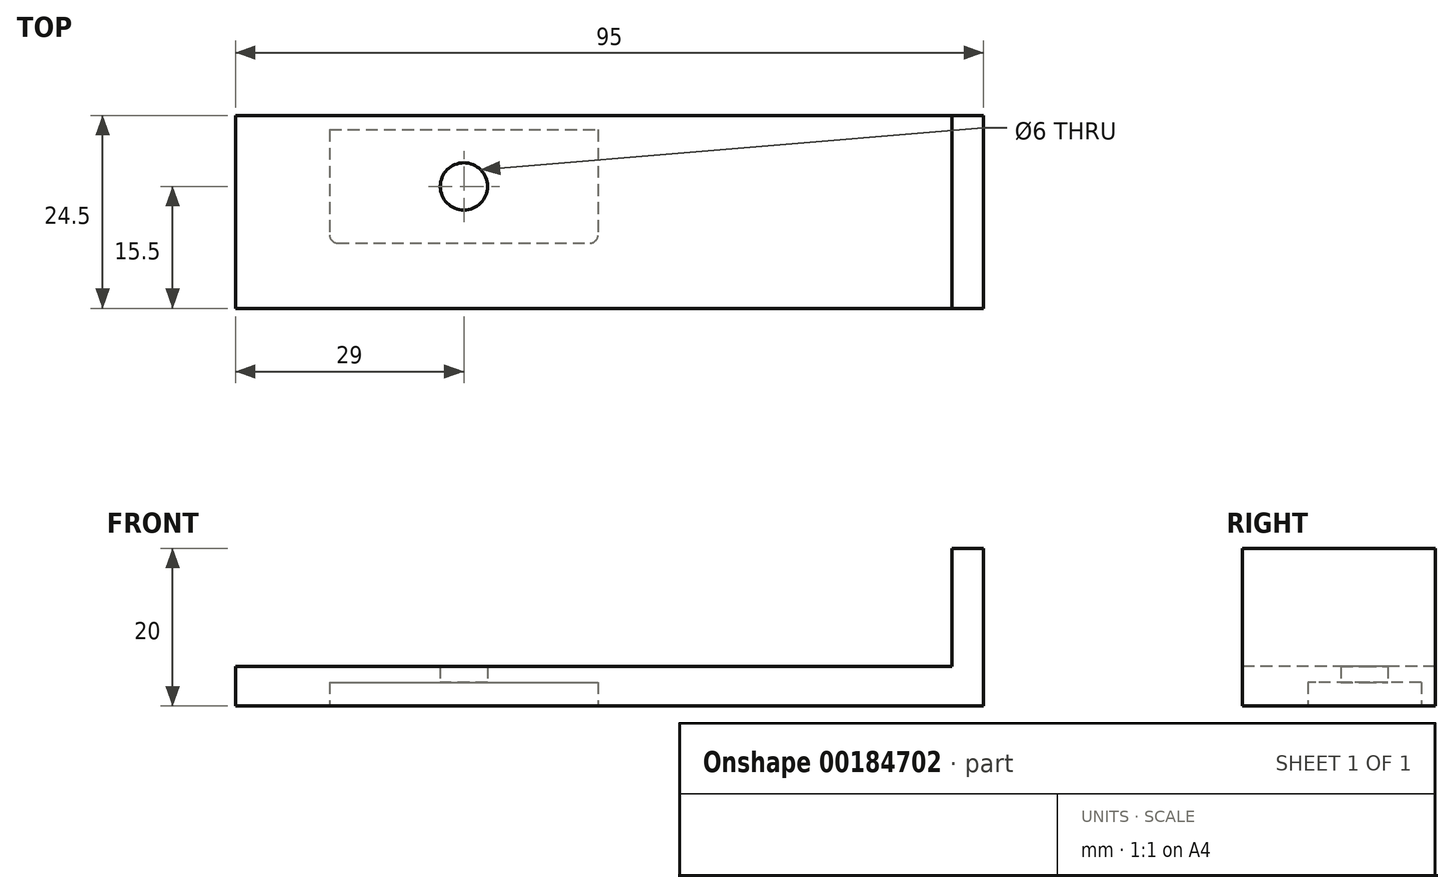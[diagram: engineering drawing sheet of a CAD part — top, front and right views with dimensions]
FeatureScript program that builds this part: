
annotation { "Feature Type Name" : "Feature", "Feature Type Description" : "" }
export const myFeature = defineFeature(function(context is Context, id is Id, definition is map)
    precondition{}
    {
        {
            var Q0;
            Q0=qCreatedBy(makeId("Top.planeOp"),FACE);
            var sketch = newSketch(context, id + "F0", { "sketchPlane" : qUnion([Q0])});
            skLineSegment(sketch, "E0.bottom", {"start": v(0, 0) * mm, "end": v(99, 0) * mm});
            skLineSegment(sketch, "E0.top", {"start": v(0, 24.5) * mm, "end": v(99, 24.5) * mm});
            skLineSegment(sketch, "E0.left", {"start": v(0, 0) * mm, "end": v(0, 24.5) * mm});
            skLineSegment(sketch, "E0.right", {"start": v(99, 0) * mm, "end": v(99, 24.5) * mm});
            skLineSegment(sketch, "E1", {"start": v(49.5, 0) * mm, "end": v(49.5, 24.5) * mm, "construction": true});
            skLineSegment(sketch, "E2.bottom", {"start": v(0, 24.5) * mm, "end": v(4, 24.5) * mm});
            skLineSegment(sketch, "E2.top", {"start": v(0, 0) * mm, "end": v(4, 0) * mm});
            skLineSegment(sketch, "E2.left", {"start": v(0, 24.5) * mm, "end": v(0, 0) * mm});
            skLineSegment(sketch, "E2.right", {"start": v(4, 24.5) * mm, "end": v(4, 0) * mm});
            skLineSegment(sketch, "E3.MirrorCS", {"start": v(95, 24.5) * mm, "end": v(95, 0) * mm});
            skLineSegment(sketch, "E4", {"start": v(33, 0) * mm, "end": v(33, 24.5) * mm, "construction": true});
            skCircle(sketch, "E5", {"center": v(33, 15.5) * mm, "radius": 3 * mm});
            skSolve(sketch);
        }
        {
            var Q0;
            {var subQ1=sQuery(id+"F0.wireOp",EDGE,"E2.right");Q0=makeQuery(id+"F0.imprint","IMPRINT",FACE,{"disambiguationData":[TD([[makeQuery(id+"F0.imprint","IMPRINT",EDGE,{"derivedFrom":subQ1}),1.0]])]});}
            extrude(context, id + "F1", {"entities" : qUnion([Q0]), "depth" : 5 * mm});
        }
        {
            var Q0;
            Q0=makeQuery(id+"F0.imprint","IMPRINT",FACE,{"disambiguationData":[TD([[makeQuery(id+"F0.imprint","IMPRINT",EDGE,{"derivedFrom":sQuery(id+"F0.wireOp",EDGE,"E2.bottom")}),-1.0]])]});
            var Q1;
            {var subQ0=sQuery(id+"F0.wireOp",EDGE,"E0.right");Q1=makeQuery(id+"F0.imprint","IMPRINT",FACE,{"disambiguationData":[TD([[makeQuery(id+"F0.imprint","IMPRINT",EDGE,{"derivedFrom":subQ0}),1.0]])]});}
            extrude(context, id + "F2", {"entities" : qUnion([Q0, Q1]), "operationType" : NewBodyOperationType.ADD, "depth" : 20 * mm});
        }
        {
            var Q0;
            {var subQ1=sQuery(id+"F0.wireOp",EDGE,"E2.right");Q0=makeQuery(id+"F0.imprint","IMPRINT",FACE,{"disambiguationData":[TD([[makeQuery(id+"F0.imprint","IMPRINT",EDGE,{"derivedFrom":subQ1}),1.0]])]});}
            var sketch = newSketch(context, id + "F3", { "sketchPlane" : qUnion([Q0])});
            skLineSegment(sketch, "E6.bottom", {"start": v(15.95, 22.7) * mm, "end": v(50.05, 22.7) * mm});
            skLineSegment(sketch, "E6.top", {"start": v(16.95, 8.3) * mm, "end": v(49.05, 8.3) * mm});
            skLineSegment(sketch, "E6.left", {"start": v(15.95, 22.7) * mm, "end": v(15.95, 9.3) * mm});
            skLineSegment(sketch, "E6.right", {"start": v(50.05, 22.7) * mm, "end": v(50.05, 9.3) * mm});
            skPoint(sketch, "E6.middle", {"position": v(33, 15.5) * mm});
            skLineSegment(sketch, "E7.0", {"start": v(11.95, 22.7) * mm, "end": v(11.95, 4.3) * mm});
            skLineSegment(sketch, "E7.1", {"start": v(11.95, 4.3) * mm, "end": v(54.05, 4.3) * mm});
            skLineSegment(sketch, "E7.2", {"start": v(54.05, 22.7) * mm, "end": v(54.05, 4.3) * mm});
            skLineSegment(sketch, "E8", {"start": v(54.05, 22.7) * mm, "end": v(50.05, 22.7) * mm});
            skLineSegment(sketch, "E9", {"start": v(15.95, 22.7) * mm, "end": v(11.95, 22.7) * mm});
            skPoint(sketch, "E10.visualSharp", {"position": v(50.05, 8.3) * mm});
            skArc(sketch, "E10.filletArc", {"start": v(49.05, 8.3) * mm, "mid": v(49.76, 8.6) * mm, "end": v(50.05, 9.3) * mm});
            skPoint(sketch, "E11.visualSharp", {"position": v(15.95, 8.3) * mm});
            skArc(sketch, "E11.filletArc", {"start": v(15.95, 9.3) * mm, "mid": v(16.24, 8.6) * mm, "end": v(16.95, 8.3) * mm});
            skSolve(sketch);
        }
        {
            var Q0;
            Q0=makeQuery(id+"F3.imprint","IMPRINT",FACE,{"disambiguationData":[TD([[makeQuery(id+"F3.imprint","IMPRINT",EDGE,{"derivedFrom":sQuery(id+"F3.wireOp",EDGE,"E6.bottom")}),-1.0]])]});
            extrude(context, id + "F4", {"entities" : qUnion([Q0]), "operationType" : NewBodyOperationType.REMOVE, "depth" : 3 * mm});
        }
    });
